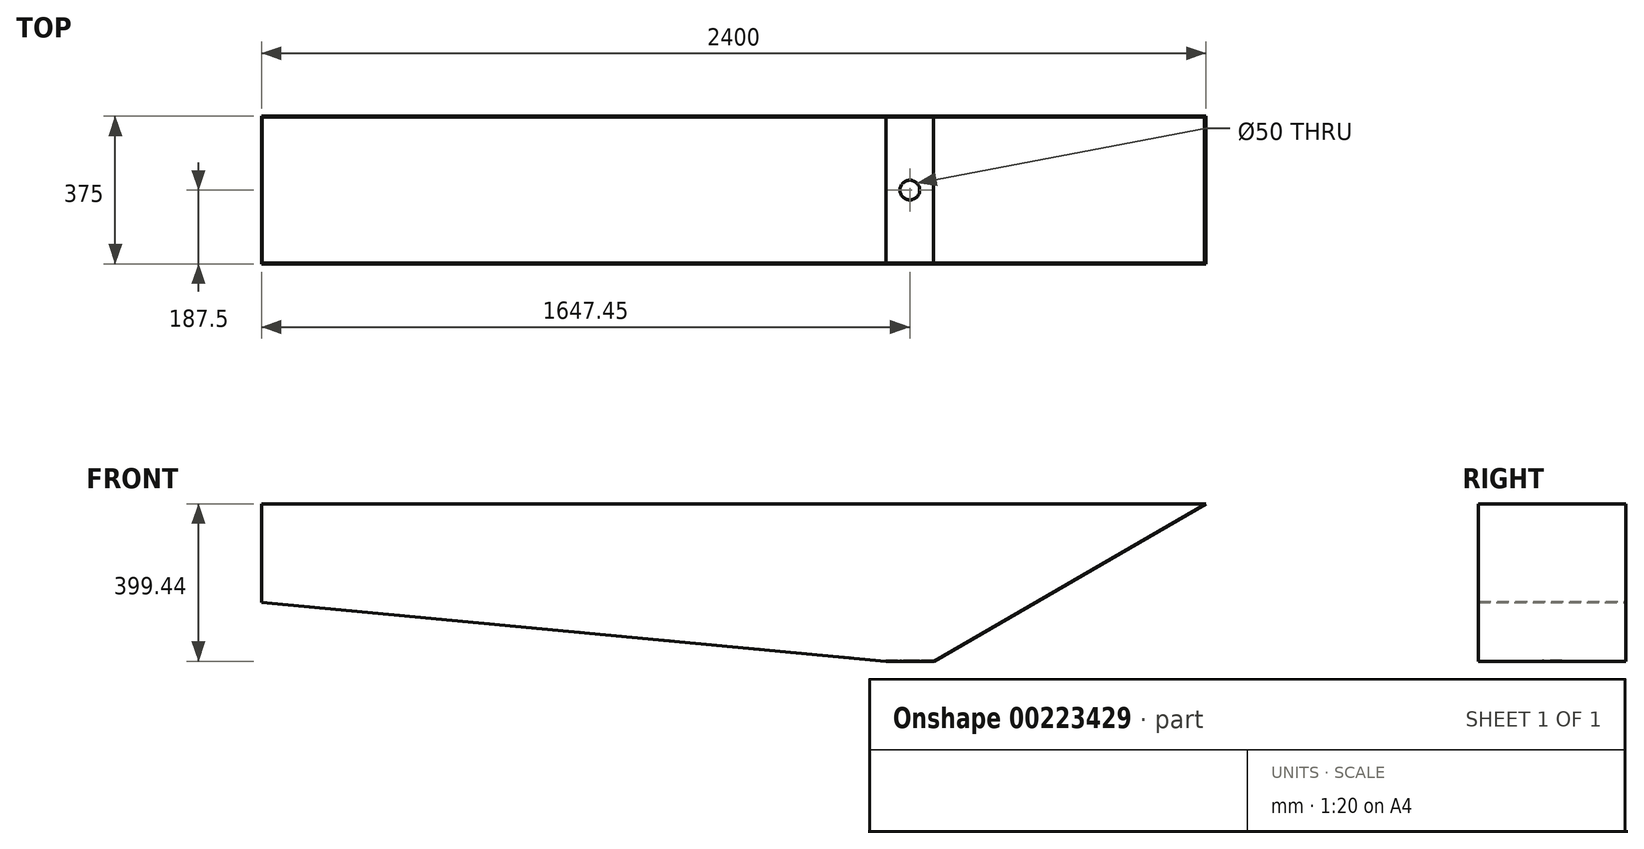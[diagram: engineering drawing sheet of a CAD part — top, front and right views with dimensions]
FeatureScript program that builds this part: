
annotation { "Feature Type Name" : "Feature", "Feature Type Description" : "" }
export const myFeature = defineFeature(function(context is Context, id is Id, definition is map)
    precondition{}
    {
        {
            var Q0;
            Q0=qCreatedBy(makeId("Front.planeOp"),FACE);
            var sketch = newSketch(context, id + "F0", { "sketchPlane" : qUnion([Q0])});
            skLineSegment(sketch, "E0", {"start": v(-1078.37, 399.44) * mm, "end": v(-1078.37, 149.44) * mm});
            skLineSegment(sketch, "E1", {"start": v(629.77, 0) * mm, "end": v(1321.63, 399.44) * mm});
            skLineSegment(sketch, "E2", {"start": v(1321.63, 399.44) * mm, "end": v(-1078.37, 399.44) * mm});
            skLineSegment(sketch, "E3", {"start": v(-1334.51, 0) * mm, "end": v(1339.5, 0) * mm, "construction": true});
            skLineSegment(sketch, "E4", {"start": v(629.77, 0) * mm, "end": v(508.83, 0) * mm});
            skLineSegment(sketch, "E5", {"start": v(-1078.37, 149.44) * mm, "end": v(508.83, 0) * mm});
            skSolve(sketch);
        }
        {
            var Q0;
            Q0=makeQuery(id+"F0.imprint","IMPRINT",FACE,{"disambiguationData":[TD([[makeQuery(id+"F0.imprint","IMPRINT",EDGE,{"derivedFrom":sQuery(id+"F0.wireOp",EDGE,"E0")}),1.0]])]});
            extrude(context, id + "F1", {"entities" : qUnion([Q0]), "depth" : 375 * mm});
        }
        {
            var Q0;
            Q0=makeQuery(id+"F1.opExtrude","SWEPT_FACE",FACE,{"disambiguationData":[OSD([sQuery(id+"F0.wireOp",EDGE,"E2")])]});
            shell(context, id + "F2", {"entities" : qUnion([Q0]), "thickness" : 2 * mm});
        }
        {
            var Q0;
            Q0=makeQuery(id+"F2.opShell","OFFSET_FACE",FACE,{"disambiguationData":[OSD([sQuery(id+"F0.wireOp",EDGE,"E4")])]});
            var sketch = newSketch(context, id + "F3", { "sketchPlane" : qUnion([Q0])});
            skLineSegment(sketch, "E6", {"start": v(508.92, -187.5) * mm, "end": v(629.23, -187.5) * mm, "construction": true});
            skLineSegment(sketch, "E7", {"start": v(569.08, -2) * mm, "end": v(569.08, -373) * mm, "construction": true});
            skCircle(sketch, "E8", {"center": v(569.08, -187.5) * mm, "radius": 25 * mm});
            skSolve(sketch);
        }
        {
            var Q0;
            Q0=makeQuery(id+"F3.imprint","IMPRINT",FACE,{"disambiguationData":[TD([[makeQuery(id+"F3.imprint","IMPRINT",EDGE,{"derivedFrom":sQuery(id+"F3.wireOp",EDGE,"E8")}),1.0]])]});
            extrude(context, id + "F4", {"entities" : qUnion([Q0]), "operationType" : NewBodyOperationType.REMOVE, "oppositeDirection" : true, "depth" : 25 * mm});
        }
    });
